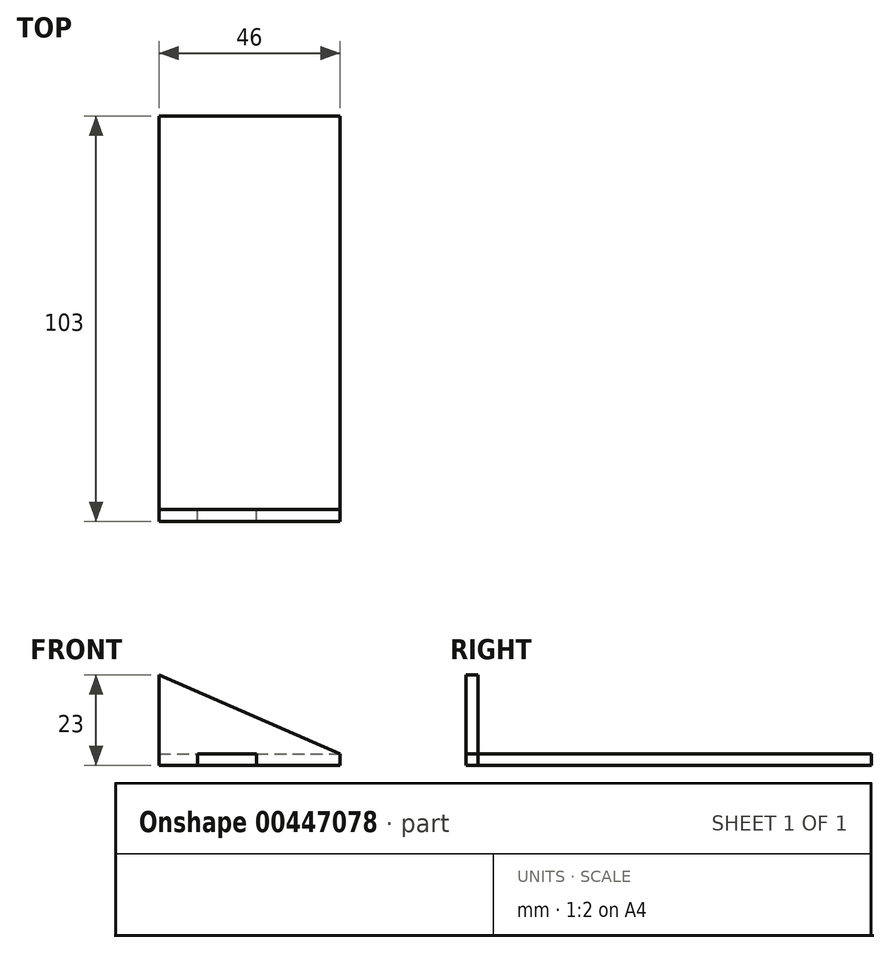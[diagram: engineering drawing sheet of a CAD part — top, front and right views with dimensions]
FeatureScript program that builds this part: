
annotation { "Feature Type Name" : "Feature", "Feature Type Description" : "" }
export const myFeature = defineFeature(function(context is Context, id is Id, definition is map)
    precondition{}
    {
        {
            var Q0;
            Q0=qCreatedBy(makeId("Front.planeOp"),FACE);
            var sketch = newSketch(context, id + "F0", { "sketchPlane" : qUnion([Q0])});
            skLineSegment(sketch, "E0", {"start": v(0, 0) * mm, "end": v(-46, 0) * mm});
            skLineSegment(sketch, "E1", {"start": v(-46, 0) * mm, "end": v(-46, 20) * mm});
            skLineSegment(sketch, "E2", {"start": v(-46, 20) * mm, "end": v(0, 0) * mm});
            skLineSegment(sketch, "E3.bottom", {"start": v(-36.24, 3) * mm, "end": v(-21.24, 3) * mm});
            skLineSegment(sketch, "E3.top", {"start": v(-36.24, -3) * mm, "end": v(-21.24, -3) * mm});
            skLineSegment(sketch, "E3.left", {"start": v(-36.24, 3) * mm, "end": v(-36.24, -3) * mm});
            skLineSegment(sketch, "E3.right", {"start": v(-21.24, 3) * mm, "end": v(-21.24, -3) * mm});
            skPoint(sketch, "E3.middle", {"position": v(-28.74, 0) * mm});
            skLineSegment(sketch, "E4", {"start": v(-46, -3) * mm, "end": v(-36.24, -3) * mm});
            skLineSegment(sketch, "E5", {"start": v(-21.24, -3) * mm, "end": v(0, -3) * mm});
            skLineSegment(sketch, "E6", {"start": v(0, -3) * mm, "end": v(0, 0) * mm});
            skLineSegment(sketch, "E7", {"start": v(-46, 0) * mm, "end": v(-46, -3) * mm});
            skSolve(sketch);
        }
        {
            var Q0;
            {var subQ1=sQuery(id+"F0.wireOp",EDGE,"E1");Q0=makeQuery(id+"F0.imprint","IMPRINT",FACE,{"disambiguationData":[TD([[makeQuery(id+"F0.imprint","IMPRINT",EDGE,{"derivedFrom":subQ1}),-1.0]])]});}
            var Q1;
            {var subQ5=sQuery(id+"F0.wireOp",EDGE,"E3.bottom");Q1=makeQuery(id+"F0.imprint","IMPRINT",FACE,{"disambiguationData":[TD([[makeQuery(id+"F0.imprint","IMPRINT",EDGE,{"derivedFrom":subQ5}),-1.0]])]});}
            var Q2;
            {var subQ4=sQuery(id+"F0.wireOp",EDGE,"E4");Q2=makeQuery(id+"F0.imprint","IMPRINT",FACE,{"disambiguationData":[TD([[makeQuery(id+"F0.imprint","IMPRINT",EDGE,{"derivedFrom":subQ4}),1.0]])]});}
            var Q3;
            {var subQ4=sQuery(id+"F0.wireOp",EDGE,"E5");Q3=makeQuery(id+"F0.imprint","IMPRINT",FACE,{"disambiguationData":[TD([[makeQuery(id+"F0.imprint","IMPRINT",EDGE,{"derivedFrom":subQ4}),1.0]])]});}
            extrude(context, id + "F1", {"entities" : qUnion([Q0, Q1, Q2, Q3]), "depth" : 3 * mm, "offsetDistance" : 25 * mm});
        }
        {
            var Q0;
            Q0=qCreatedBy(makeId("Top.planeOp"),FACE);
            var sketch = newSketch(context, id + "F2", { "sketchPlane" : qUnion([Q0])});
            skLineSegment(sketch, "E8.0", {"start": v(-36.24, -3) * mm, "end": v(-36.24, 0) * mm});
            skLineSegment(sketch, "E9.0", {"start": v(-21.24, -3) * mm, "end": v(-36.24, -3) * mm});
            skLineSegment(sketch, "E10.0", {"start": v(-21.24, -3) * mm, "end": v(-21.24, 0) * mm});
            skLineSegment(sketch, "E11.0", {"start": v(-46, 0) * mm, "end": v(-36.24, 0) * mm});
            skLineSegment(sketch, "E12.0", {"start": v(-21.24, 0) * mm, "end": v(0, 0) * mm});
            skPoint(sketch, "E13.0", {"position": v(-46, 0) * mm});
            skLineSegment(sketch, "E14", {"start": v(-46, 0) * mm, "end": v(0, 0) * mm, "construction": true});
            skLineSegment(sketch, "E15.bottom", {"start": v(-46, -100) * mm, "end": v(0, -100) * mm});
            skLineSegment(sketch, "E15.top", {"start": v(-46, 100) * mm, "end": v(0, 100) * mm});
            skLineSegment(sketch, "E15.left", {"start": v(-46, 0) * mm, "end": v(-46, 100) * mm});
            skLineSegment(sketch, "E15.right", {"start": v(0, 0) * mm, "end": v(0, 100) * mm});
            skPoint(sketch, "E15.middle", {"position": v(-23, 0) * mm});
            skSolve(sketch);
        }
        {
            var Q0;
            Q0 = qSketchRegion(id + "F2", true);
            extrude(context, id + "F3", {"entities" : qUnion([Q0]), "oppositeDirection" : true, "depth" : 3 * mm, "offsetDistance" : 25 * mm});
        }
    });
